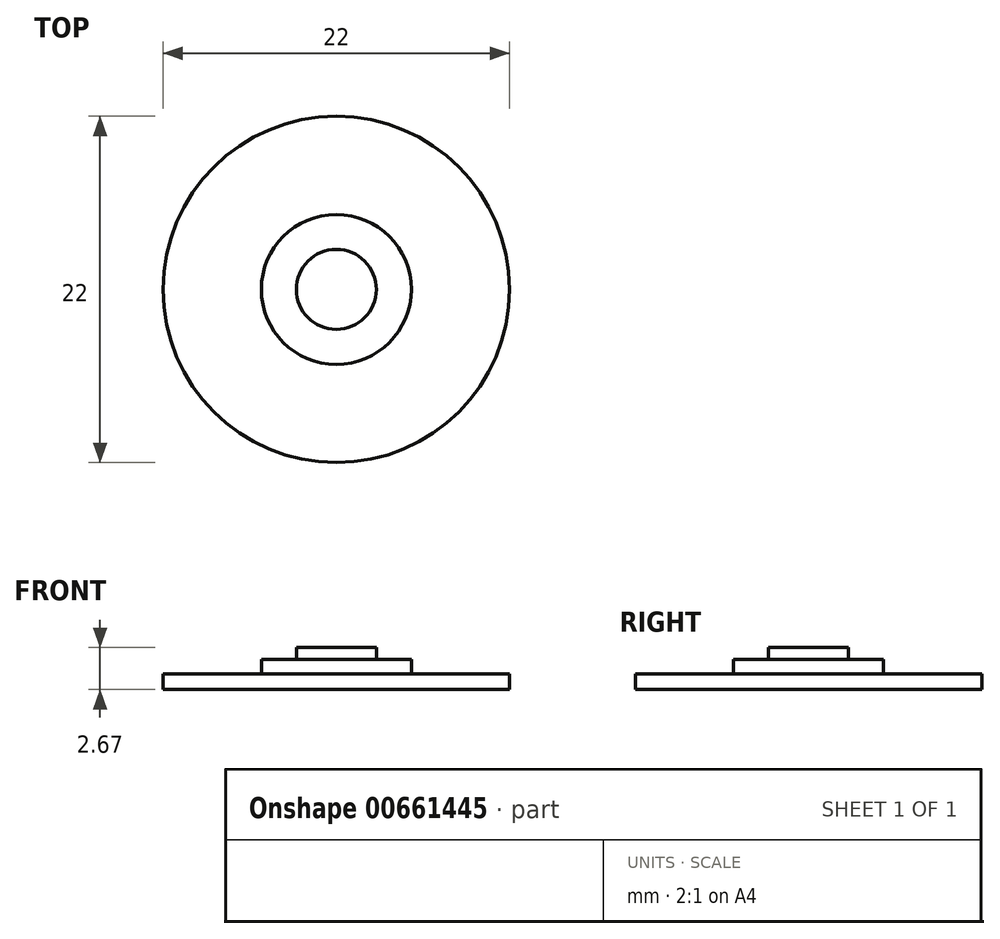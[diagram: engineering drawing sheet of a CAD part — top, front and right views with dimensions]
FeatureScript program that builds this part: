
annotation { "Feature Type Name" : "Feature", "Feature Type Description" : "" }
export const myFeature = defineFeature(function(context is Context, id is Id, definition is map)
    precondition{}
    {
        {
            var Q0;
            Q0=qCreatedBy(makeId("Top.planeOp"),FACE);
            var sketch = newSketch(context, id + "F0", { "sketchPlane" : qUnion([Q0])});
            skCircle(sketch, "E0", {"center": v(0, 0) * mm, "radius": 4.76 * mm});
            skCircle(sketch, "E1", {"center": v(0, 0) * mm, "radius": 2.61 * mm});
            skCircle(sketch, "E2", {"center": v(0, 0) * mm, "radius": 11 * mm});
            skSolve(sketch);
        }
        {
            var Q0;
            Q0=makeQuery(id+"F0.imprint","IMPRINT",FACE,{"disambiguationData":[TD([[makeQuery(id+"F0.imprint","IMPRINT",EDGE,{"derivedFrom":sQuery(id+"F0.wireOp",EDGE,"E0")}),1.0]])]});
            var Q1;
            Q1=makeQuery(id+"F0.imprint","IMPRINT",FACE,{"disambiguationData":[TD([[makeQuery(id+"F0.imprint","IMPRINT",EDGE,{"derivedFrom":sQuery(id+"F0.wireOp",EDGE,"E1")}),1.0]])]});
            extrude(context, id + "F1", {"entities" : qUnion([Q0, Q1]), "depth" : 1.93 * mm, "offsetDistance" : 25.4 * mm});
        }
        {
            var Q0;
            Q0=makeQuery(id+"F0.imprint","IMPRINT",FACE,{"disambiguationData":[TD([[makeQuery(id+"F0.imprint","IMPRINT",EDGE,{"derivedFrom":sQuery(id+"F0.wireOp",EDGE,"E0")}),-1.0]])]});
            var Q1;
            Q1=sQuery(id+"F0.wireOp",EDGE,"E1");
            extrude(context, id + "F2", {"entities" : qUnion([Q0]), "operationType" : NewBodyOperationType.ADD, "surfaceEntities" : qUnion([Q1]), "depth" : 1 * mm, "offsetDistance" : 25.4 * mm});
        }
        {
            var Q0;
            Q0=makeQuery(id+"F1.opExtrude","CAP_FACE",FACE,{"disambiguationData":[OSD([sQuery(id+"F0.wireOp",EDGE,"E0")])],"isStart":false});
            var sketch = newSketch(context, id + "F3", { "sketchPlane" : qUnion([Q0])});
            skCircle(sketch, "E3", {"center": v(0, 0) * mm, "radius": 2.54 * mm});
            skSolve(sketch);
        }
        {
            var Q0;
            Q0=makeQuery(id+"F3.imprint","IMPRINT",FACE,{"disambiguationData":[TD([[makeQuery(id+"F3.imprint","IMPRINT",EDGE,{"derivedFrom":sQuery(id+"F3.wireOp",EDGE,"E3")}),1.0]])]});
            var Q1;
            Q1=sQuery(id+"F3.wireOp",EDGE,"E3");
            extrude(context, id + "F4", {"entities" : qUnion([Q0]), "operationType" : NewBodyOperationType.ADD, "surfaceEntities" : qUnion([Q1]), "depth" : 0.74 * mm, "offsetDistance" : 25.4 * mm});
        }
    });
